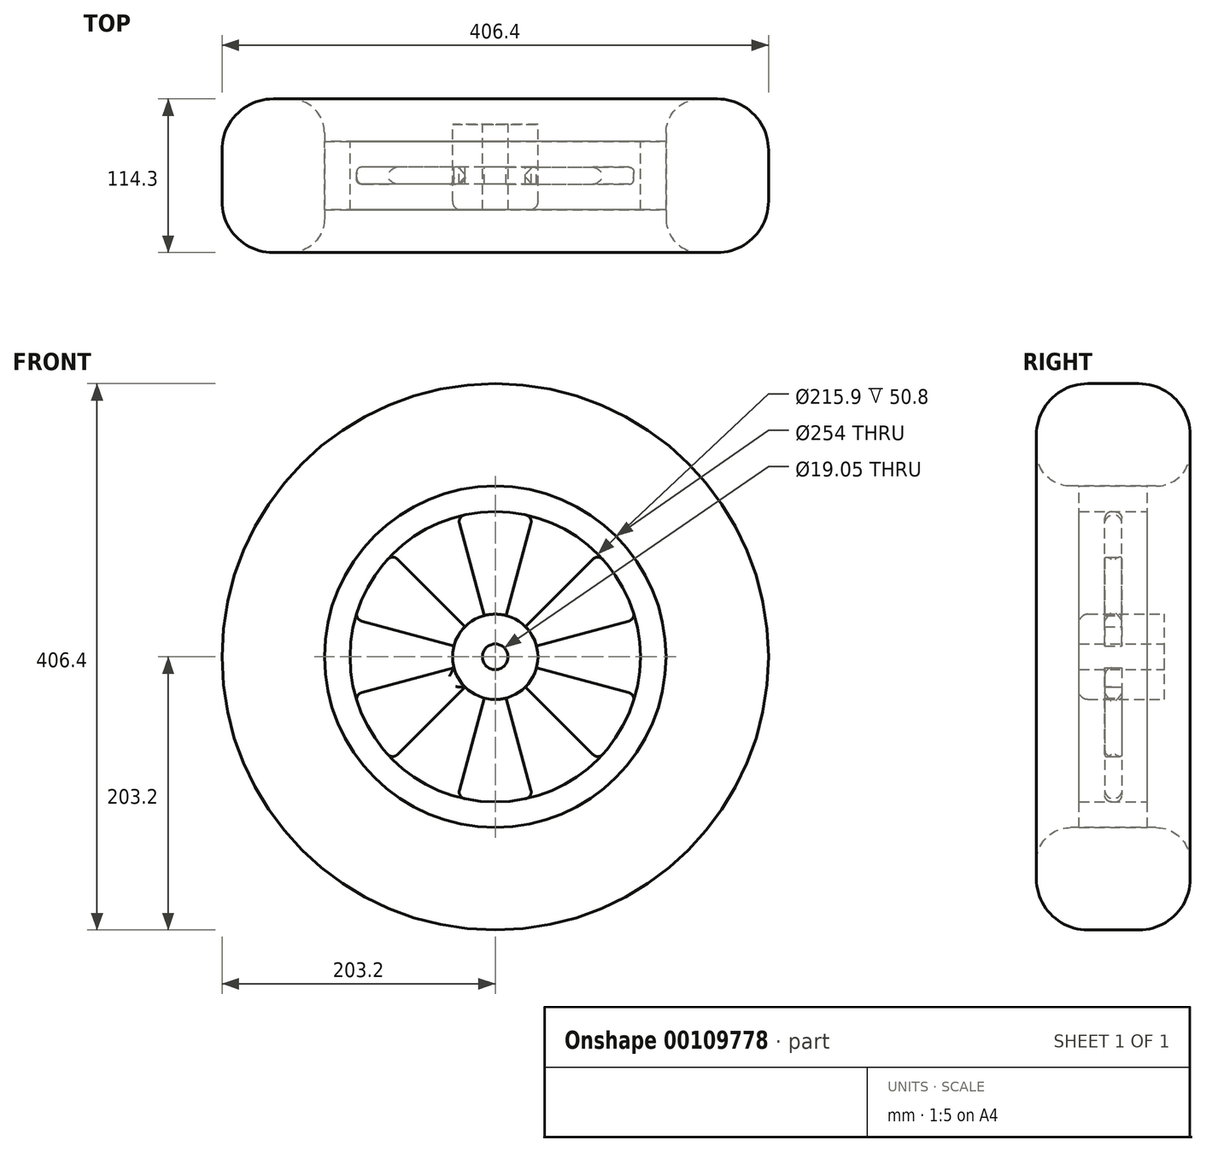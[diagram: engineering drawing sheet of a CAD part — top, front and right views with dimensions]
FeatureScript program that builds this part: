
annotation { "Feature Type Name" : "Feature", "Feature Type Description" : "" }
export const myFeature = defineFeature(function(context is Context, id is Id, definition is map)
    precondition{}
    {
        {
            var Q0;
            Q0=qCreatedBy(makeId("Front.planeOp"),FACE);
            var sketch = newSketch(context, id + "F0", { "sketchPlane" : qUnion([Q0])});
            skCircle(sketch, "E0", {"center": v(0, 0) * mm, "radius": 203.2 * mm});
            skCircle(sketch, "E1", {"center": v(0, 0) * mm, "radius": 127 * mm});
            skSolve(sketch);
        }
        {
            var Q0;
            Q0 = qSketchRegion(id + "F0", true);
            extrude(context, id + "F1", {"entities" : qUnion([Q0]), "endBound" : BoundingType.SYMMETRIC, "oppositeDirection" : true, "depth" : 114.3 * mm});
        }
        {
            var Q0;
            Q0=makeQuery(id+"F1.opExtrude","CAP_EDGE",EDGE,{"disambiguationData":[OSD([sQuery(id+"F0.wireOp",EDGE,"E0")])],"isStart":true});
            var Q1;
            Q1=makeQuery(id+"F1.opExtrude","CAP_EDGE",EDGE,{"disambiguationData":[OSD([sQuery(id+"F0.wireOp",EDGE,"E0")])],"isStart":false});
            var Q2;
            Q2=makeQuery(id+"F1.opExtrude","CAP_EDGE",EDGE,{"disambiguationData":[OSD([sQuery(id+"F0.wireOp",EDGE,"lpEB0Qa2-3oW2-Fq1t-q1Yl-T2NJAg49ok8W")])],"isStart":true});
            var Q3;
            Q3=makeQuery(id+"F1.opExtrude","CAP_EDGE",EDGE,{"disambiguationData":[OSD([sQuery(id+"F0.wireOp",EDGE,"lpEB0Qa2-3oW2-Fq1t-q1Yl-T2NJAg49ok8W")])],"isStart":false});
            fillet(context, id + "F2", {"entities" : qUnion([Q0, Q1, Q2, Q3]), "radius" : 38.1 * mm, "tangentPropagation" : true, "allowEdgeOverflow" : false});
        }
        {
            var Q0;
            Q0=makeQuery(id+"F1.opExtrude","CAP_EDGE",EDGE,{"disambiguationData":[OSD([sQuery(id+"F0.wireOp",EDGE,"E1")])],"isStart":false});
            var Q1;
            Q1=makeQuery(id+"F1.opExtrude","CAP_EDGE",EDGE,{"disambiguationData":[OSD([sQuery(id+"F0.wireOp",EDGE,"E1")])],"isStart":true});
            fillet(context, id + "F3", {"entities" : qUnion([Q0, Q1]), "radius" : 25.4 * mm, "tangentPropagation" : true, "allowEdgeOverflow" : false});
        }
        {
            var Q0;
            Q0=makeQuery(id+"F0.imprint","IMPRINT",FACE,{"disambiguationData":[TD([[makeQuery(id+"F0.imprint","IMPRINT",EDGE,{"derivedFrom":sQuery(id+"F0.wireOp",EDGE,"E1")}),1.0]])]});
            var sketch = newSketch(context, id + "F4", { "sketchPlane" : qUnion([Q0])});
            skCircle(sketch, "E2", {"center": v(0, 0) * mm, "radius": 127 * mm});
            skCircle(sketch, "E3", {"center": v(0, 0) * mm, "radius": 107.95 * mm});
            skSolve(sketch);
        }
        {
            var Q0;
            Q0 = qSketchRegion(id + "F4", true);
            extrude(context, id + "F5", {"entities" : qUnion([Q0]), "endBound" : BoundingType.SYMMETRIC, "depth" : 50.8 * mm});
        }
        {
            var Q0;
            Q0=makeQuery(id+"F0.imprint","IMPRINT",FACE,{"disambiguationData":[TD([[makeQuery(id+"F0.imprint","IMPRINT",EDGE,{"derivedFrom":sQuery(id+"F0.wireOp",EDGE,"E1")}),1.0]])]});
            var sketch = newSketch(context, id + "F6", { "sketchPlane" : qUnion([Q0])});
            skCircle(sketch, "E4", {"center": v(0, 0) * mm, "radius": 31.75 * mm});
            skCircle(sketch, "E5", {"center": v(0, 0) * mm, "radius": 9.53 * mm});
            skSolve(sketch);
        }
        {
            var Q0;
            Q0 = qSketchRegion(id + "F6", true);
            extrude(context, id + "F7", {"entities" : qUnion([Q0]), "depth" : 25.4 * mm, "hasSecondDirection" : true, "secondDirectionOppositeDirection" : true, "secondDirectionDepth" : 38.1 * mm});
        }
        {
            var Q0;
            Q0=makeQuery(id+"F0.imprint","IMPRINT",FACE,{"disambiguationData":[TD([[makeQuery(id+"F0.imprint","IMPRINT",EDGE,{"derivedFrom":sQuery(id+"F0.wireOp",EDGE,"E1")}),1.0]])]});
            var sketch = newSketch(context, id + "F8", { "sketchPlane" : qUnion([Q0])});
            skLineSegment(sketch, "E6", {"start": v(-8.22, 30.67) * mm, "end": v(-27.94, 104.27) * mm});
            skLineSegment(sketch, "E7.MirrorCS", {"start": v(8.22, 30.67) * mm, "end": v(27.96, 104.35) * mm});
            skLineSegment(sketch, "E8.MirrorCS", {"start": v(-8.22, -30.67) * mm, "end": v(-27.96, -104.35) * mm});
            skLineSegment(sketch, "E9.MirrorCS", {"start": v(8.22, -30.67) * mm, "end": v(27.96, -104.35) * mm});
            skLineSegment(sketch, "E10", {"start": v(-22.45, 22.45) * mm, "end": v(-76.33, 76.33) * mm});
            skLineSegment(sketch, "E11", {"start": v(-30.67, 8.22) * mm, "end": v(-104.27, 27.94) * mm});
            skLineSegment(sketch, "E12.MirrorCS", {"start": v(-22.45, -22.45) * mm, "end": v(-76.33, -76.33) * mm});
            skLineSegment(sketch, "E13.MirrorCS", {"start": v(-30.67, -8.22) * mm, "end": v(-104.27, -27.94) * mm});
            skLineSegment(sketch, "E14.MirrorCS", {"start": v(22.45, 22.45) * mm, "end": v(76.33, 76.33) * mm});
            skLineSegment(sketch, "E15.MirrorCS", {"start": v(30.67, 8.22) * mm, "end": v(104.27, 27.94) * mm});
            skArc(sketch, "E16", {"start": v(-76.33, 76.33) * mm, "mid": v(-93.49, 53.97) * mm, "end": v(-104.27, 27.94) * mm});
            skPoint(sketch, "E17.orphan", {"position": v(-75.6, 75.6) * mm});
            skPoint(sketch, "E18.orphan", {"position": v(-27.96, 104.35) * mm});
            skPoint(sketch, "E19.orphan", {"position": v(-75.6, -75.6) * mm});
            skArc(sketch, "E20.trimOffspring", {"start": v(-104.27, -27.94) * mm, "mid": v(-93.49, -53.97) * mm, "end": v(-76.33, -76.33) * mm});
            skArc(sketch, "E21.trimOffspring", {"start": v(-27.94, -104.27) * mm, "mid": v(0, -107.95) * mm, "end": v(27.94, -104.27) * mm});
            skArc(sketch, "E22.trimOffspring", {"start": v(27.94, 104.27) * mm, "mid": v(0, 107.95) * mm, "end": v(-27.94, 104.27) * mm});
            skArc(sketch, "E23", {"start": v(-22.45, 22.45) * mm, "mid": v(-27.5, 15.87) * mm, "end": v(-30.67, 8.22) * mm});
            skPoint(sketch, "E24.orphan", {"position": v(75.6, 75.6) * mm});
            skArc(sketch, "E25.trimOffspring", {"start": v(-30.67, -8.22) * mm, "mid": v(-27.5, -15.87) * mm, "end": v(-22.45, -22.45) * mm});
            skArc(sketch, "E26.trimOffspring", {"start": v(-8.22, -30.67) * mm, "mid": v(0, -31.75) * mm, "end": v(8.22, -30.67) * mm});
            skArc(sketch, "E27.trimOffspring", {"start": v(30.67, 8.22) * mm, "mid": v(27.5, 15.87) * mm, "end": v(22.45, 22.45) * mm});
            skArc(sketch, "E28.trimOffspring", {"start": v(8.22, 30.67) * mm, "mid": v(0, 31.75) * mm, "end": v(-8.22, 30.67) * mm});
            skLineSegment(sketch, "E29.MirrorCS", {"start": v(30.67, -8.22) * mm, "end": v(104.27, -27.94) * mm});
            skArc(sketch, "E30.MirrorCS", {"start": v(104.27, -27.94) * mm, "mid": v(93.49, -53.97) * mm, "end": v(76.33, -76.33) * mm});
            skLineSegment(sketch, "E31.MirrorCS", {"start": v(22.45, -22.45) * mm, "end": v(76.33, -76.33) * mm});
            skArc(sketch, "E32.MirrorCS", {"start": v(30.67, -8.22) * mm, "mid": v(27.5, -15.87) * mm, "end": v(22.45, -22.45) * mm});
            skArc(sketch, "E33.MirrorCS", {"start": v(76.33, 76.33) * mm, "mid": v(93.49, 53.97) * mm, "end": v(104.27, 27.94) * mm});
            skSolve(sketch);
        }
        {
            var Q0;
            Q0 = qSketchRegion(id + "F8", true);
            extrude(context, id + "F9", {"entities" : qUnion([Q0]), "endBound" : BoundingType.SYMMETRIC, "depth" : 12.7 * mm});
        }
        {
            var Q0;
            Q0=makeQuery(id+"F9.opExtrude","CAP_EDGE",EDGE,{"disambiguationData":[OSD([sQuery(id+"F8.wireOp",EDGE,"E21.trimOffspring")])],"isStart":false});
            var Q1;
            Q1=makeQuery(id+"F9.opExtrude","CAP_EDGE",EDGE,{"disambiguationData":[OSD([sQuery(id+"F8.wireOp",EDGE,"E30.MirrorCS")])],"isStart":false});
            var Q2;
            Q2=makeQuery(id+"F9.opExtrude","CAP_EDGE",EDGE,{"disambiguationData":[OSD([sQuery(id+"F8.wireOp",EDGE,"E33.MirrorCS")])],"isStart":false});
            var Q3;
            Q3=makeQuery(id+"F9.opExtrude","CAP_EDGE",EDGE,{"disambiguationData":[OSD([sQuery(id+"F8.wireOp",EDGE,"E22.trimOffspring")])],"isStart":false});
            var Q4;
            Q4=makeQuery(id+"F9.opExtrude","CAP_EDGE",EDGE,{"disambiguationData":[OSD([sQuery(id+"F8.wireOp",EDGE,"E16")])],"isStart":false});
            var Q5;
            Q5=makeQuery(id+"F9.opExtrude","CAP_FACE",FACE,{"disambiguationData":[OSD([sQuery(id+"F8.wireOp",EDGE,"E12.MirrorCS"),sQuery(id+"F8.wireOp",EDGE,"E13.MirrorCS"),sQuery(id+"F8.wireOp",EDGE,"E20.trimOffspring"),sQuery(id+"F8.wireOp",EDGE,"E25.trimOffspring")])],"isStart":false});
            var Q6;
            Q6=makeQuery(id+"F9.opExtrude","CAP_EDGE",EDGE,{"disambiguationData":[OSD([sQuery(id+"F8.wireOp",EDGE,"E16")])],"isStart":true});
            var Q7;
            Q7=makeQuery(id+"F9.opExtrude","CAP_EDGE",EDGE,{"disambiguationData":[OSD([sQuery(id+"F8.wireOp",EDGE,"E22.trimOffspring")])],"isStart":true});
            var Q8;
            Q8=makeQuery(id+"F9.opExtrude","CAP_EDGE",EDGE,{"disambiguationData":[OSD([sQuery(id+"F8.wireOp",EDGE,"E20.trimOffspring")])],"isStart":true});
            var Q9;
            Q9=makeQuery(id+"F9.opExtrude","CAP_EDGE",EDGE,{"disambiguationData":[OSD([sQuery(id+"F8.wireOp",EDGE,"E21.trimOffspring")])],"isStart":true});
            var Q10;
            Q10=makeQuery(id+"F9.opExtrude","CAP_EDGE",EDGE,{"disambiguationData":[OSD([sQuery(id+"F8.wireOp",EDGE,"E30.MirrorCS")])],"isStart":true});
            var Q11;
            Q11=makeQuery(id+"F9.opExtrude","CAP_EDGE",EDGE,{"disambiguationData":[OSD([sQuery(id+"F8.wireOp",EDGE,"E33.MirrorCS")])],"isStart":true});
            var Q12;
            Q12=makeQuery(id+"F9.opExtrude","SWEPT_EDGE",EDGE,{"disambiguationData":[OSD([sQuery(id+"F8.wireOp",EDGE,"E11"),sQuery(id+"F8.wireOp",EDGE,"E16")])]});
            var Q13;
            Q13=makeQuery(id+"F9.opExtrude","SWEPT_EDGE",EDGE,{"disambiguationData":[OSD([sQuery(id+"F8.wireOp",EDGE,"E6"),sQuery(id+"F8.wireOp",EDGE,"E22.trimOffspring")])]});
            var Q14;
            Q14=makeQuery(id+"F9.opExtrude","SWEPT_EDGE",EDGE,{"disambiguationData":[OSD([sQuery(id+"F8.wireOp",EDGE,"E13.MirrorCS"),sQuery(id+"F8.wireOp",EDGE,"E20.trimOffspring")])]});
            var Q15;
            Q15=makeQuery(id+"F9.opExtrude","SWEPT_EDGE",EDGE,{"disambiguationData":[OSD([sQuery(id+"F8.wireOp",EDGE,"E10"),sQuery(id+"F8.wireOp",EDGE,"E16")])]});
            var Q16;
            Q16=makeQuery(id+"F9.opExtrude","SWEPT_EDGE",EDGE,{"disambiguationData":[OSD([sQuery(id+"F8.wireOp",EDGE,"E7.MirrorCS"),sQuery(id+"F8.wireOp",EDGE,"E22.trimOffspring")])]});
            var Q17;
            Q17=makeQuery(id+"F9.opExtrude","SWEPT_EDGE",EDGE,{"disambiguationData":[OSD([sQuery(id+"F8.wireOp",EDGE,"E14.MirrorCS"),sQuery(id+"F8.wireOp",EDGE,"E33.MirrorCS")])]});
            var Q18;
            Q18=makeQuery(id+"F9.opExtrude","SWEPT_EDGE",EDGE,{"disambiguationData":[OSD([sQuery(id+"F8.wireOp",EDGE,"E15.MirrorCS"),sQuery(id+"F8.wireOp",EDGE,"E33.MirrorCS")])]});
            var Q19;
            Q19=makeQuery(id+"F9.opExtrude","SWEPT_EDGE",EDGE,{"disambiguationData":[OSD([sQuery(id+"F8.wireOp",EDGE,"E29.MirrorCS"),sQuery(id+"F8.wireOp",EDGE,"E30.MirrorCS")])]});
            var Q20;
            Q20=makeQuery(id+"F9.opExtrude","SWEPT_EDGE",EDGE,{"disambiguationData":[OSD([sQuery(id+"F8.wireOp",EDGE,"E30.MirrorCS"),sQuery(id+"F8.wireOp",EDGE,"E31.MirrorCS")])]});
            var Q21;
            Q21=makeQuery(id+"F9.opExtrude","SWEPT_EDGE",EDGE,{"disambiguationData":[OSD([sQuery(id+"F8.wireOp",EDGE,"E8.MirrorCS"),sQuery(id+"F8.wireOp",EDGE,"E21.trimOffspring")])]});
            var Q22;
            Q22=makeQuery(id+"F9.opExtrude","SWEPT_EDGE",EDGE,{"disambiguationData":[OSD([sQuery(id+"F8.wireOp",EDGE,"E12.MirrorCS"),sQuery(id+"F8.wireOp",EDGE,"E20.trimOffspring")])]});
            var Q23;
            Q23=makeQuery(id+"F9.opExtrude","SWEPT_EDGE",EDGE,{"disambiguationData":[OSD([sQuery(id+"F8.wireOp",EDGE,"E9.MirrorCS"),sQuery(id+"F8.wireOp",EDGE,"E21.trimOffspring")])]});
            fillet(context, id + "F10", {"entities" : qUnion([Q0, Q1, Q2, Q3, Q4, Q5, Q6, Q7, Q8, Q9, Q10, Q11, Q12, Q13, Q14, Q15, Q16, Q17, Q18, Q19, Q20, Q21, Q22, Q23]), "radius" : 5.08 * mm, "tangentPropagation" : true, "allowEdgeOverflow" : false});
        }
        {
            var Q0;
            Q0=makeQuery(id+"F7.opExtrude","CAP_EDGE",EDGE,{"disambiguationData":[OSD([sQuery(id+"F6.wireOp",EDGE,"E4")])],"isStart":false});
            fillet(context, id + "F11", {"entities" : qUnion([Q0]), "radius" : 6.35 * mm, "tangentPropagation" : true, "allowEdgeOverflow" : false});
        }
    });
